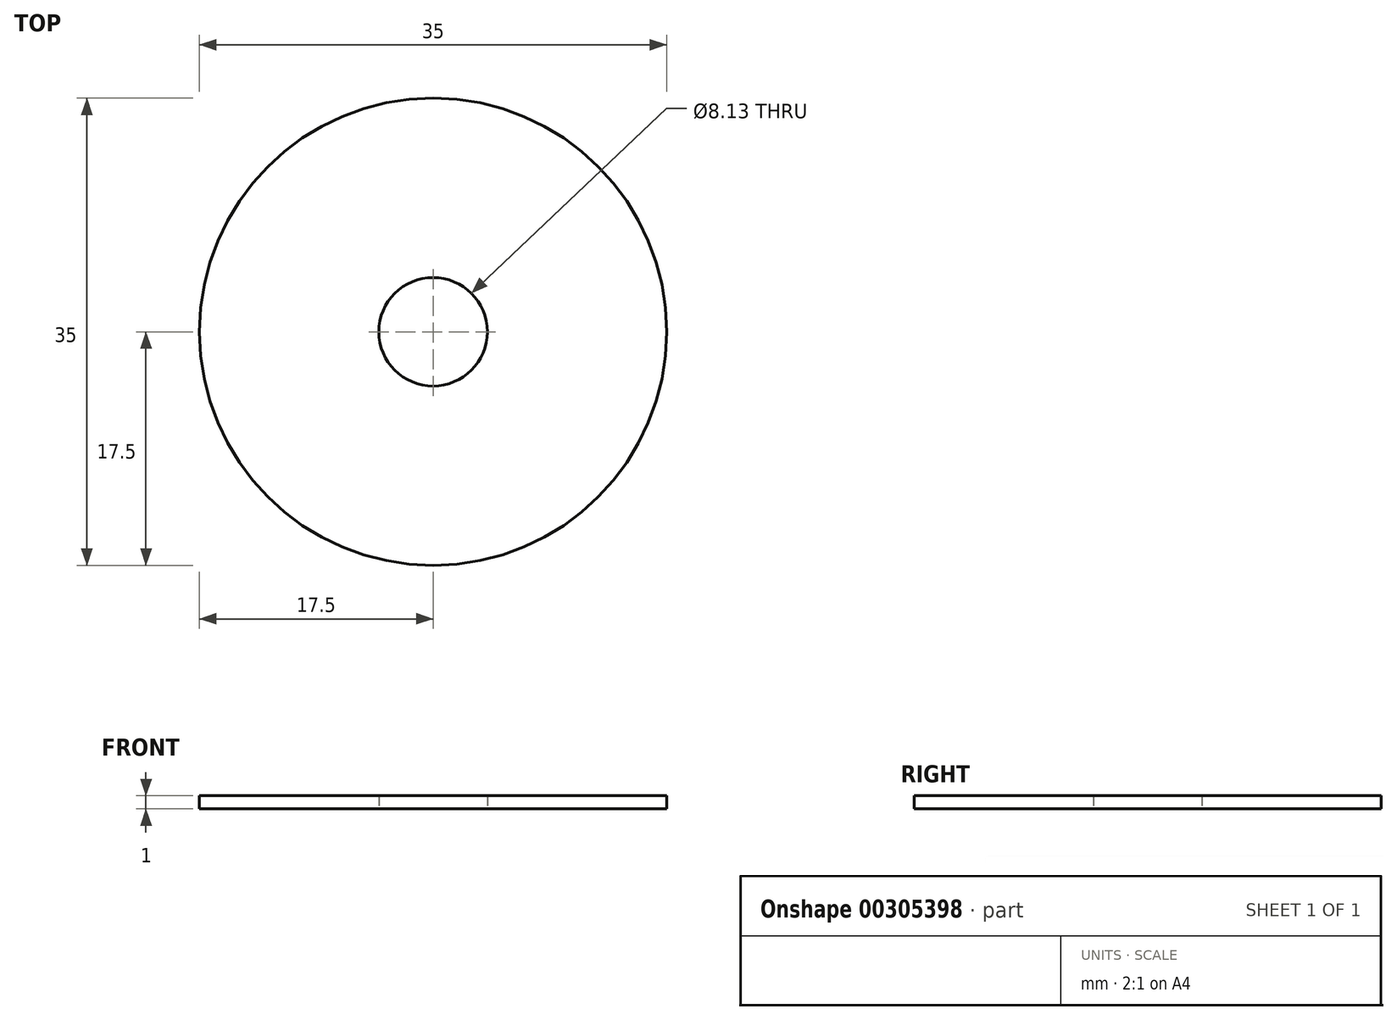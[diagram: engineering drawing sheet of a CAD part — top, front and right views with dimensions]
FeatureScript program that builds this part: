
annotation { "Feature Type Name" : "Feature", "Feature Type Description" : "" }
export const myFeature = defineFeature(function(context is Context, id is Id, definition is map)
    precondition{}
    {
        {
            var Q0;
            Q0=qCreatedBy(makeId("Front.planeOp"),FACE);
            var sketch = newSketch(context, id + "F0", { "sketchPlane" : qUnion([Q0])});
            skLineSegment(sketch, "E0", {"start": v(0, 0) * mm, "end": v(0, 10) * mm, "construction": true});
            skLineSegment(sketch, "E1.bottom", {"start": v(-4.06, 0) * mm, "end": v(-17.5, 0) * mm});
            skLineSegment(sketch, "E1.top", {"start": v(-4.06, 1) * mm, "end": v(-17.5, 1) * mm});
            skLineSegment(sketch, "E1.left", {"start": v(-4.06, 0) * mm, "end": v(-4.06, 1) * mm});
            skLineSegment(sketch, "E1.right", {"start": v(-17.5, 0) * mm, "end": v(-17.5, 1) * mm});
            skSolve(sketch);
        }
        {
            var Q0;
            Q0 = qSketchRegion(id + "F0", true);
            var Q1;
            Q1=sQuery(id+"F0.wireOp",EDGE,"E0");
            revolve(context, id + "F1", {"entities" : qUnion([Q0]), "axis" : qUnion([Q1]), "revolveType" : RevolveType.FULL});
        }
    });
